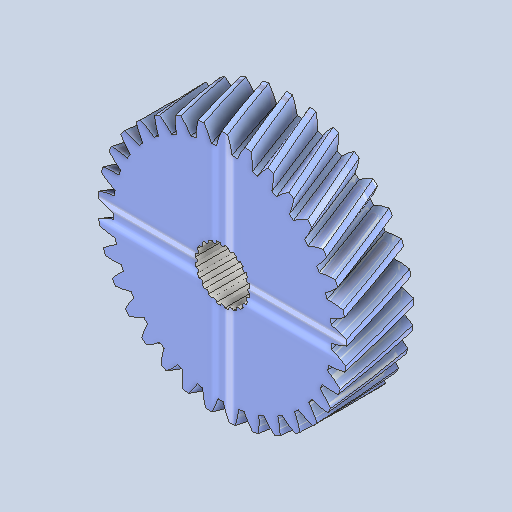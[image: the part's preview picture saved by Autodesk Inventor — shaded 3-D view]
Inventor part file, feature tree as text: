
AUTODESK INVENTOR PART (.ipt)
format: ipt  version: 2025.1 (Build 291241020, 241B)  size: 862,208 bytes
history: native  units: mm (DEFAULTED — no unit token found)
features: plane x3, other x3, extrude x2, sketch x2
ambient origin geometry x8: Origin, YZ Plane, XZ Plane, XY Plane, X Axis, Y Axis, Z Axis, Center Point
bodies: Solid1 (feature_tree)
feature tree (10):
  extrude  "Extrusion1"  Depth=15.0mm TaperAngle=0.0deg
  plane  "Work Plane2"
  plane  "Work Plane8"
  plane  "Work Plane9"
  other  "Spur Gear"
  extrude  "Extrusion2"  Depth=10.0mm TaperAngle=0.0deg
  sketch  "Sketch1"  dims[d0=55.676444mm d1=15.0mm d2=0.0mm]
  other  "Srf1"
  sketch  "Sketch Circular Pattern1"  dims[d3=52.6768mm d4=10.0mm d5=0.0mm d16=63.909111mm d17=0.0mm d34=0.951998mm d39=0.0mm d41=0.0mm d43=63.909111mm d46=63.909111mm d47=0.0mm d48=0.0mm d49=12.217mm d50=0.0mm d51=0.0mm d53=0.515mm d54=6.1135mm d55=200.0mm d57=360.0deg d59=0.5mm d60=0.872665mm d61=0.5mm d62=0.872665mm]
  other  "Pitch Diameter"
